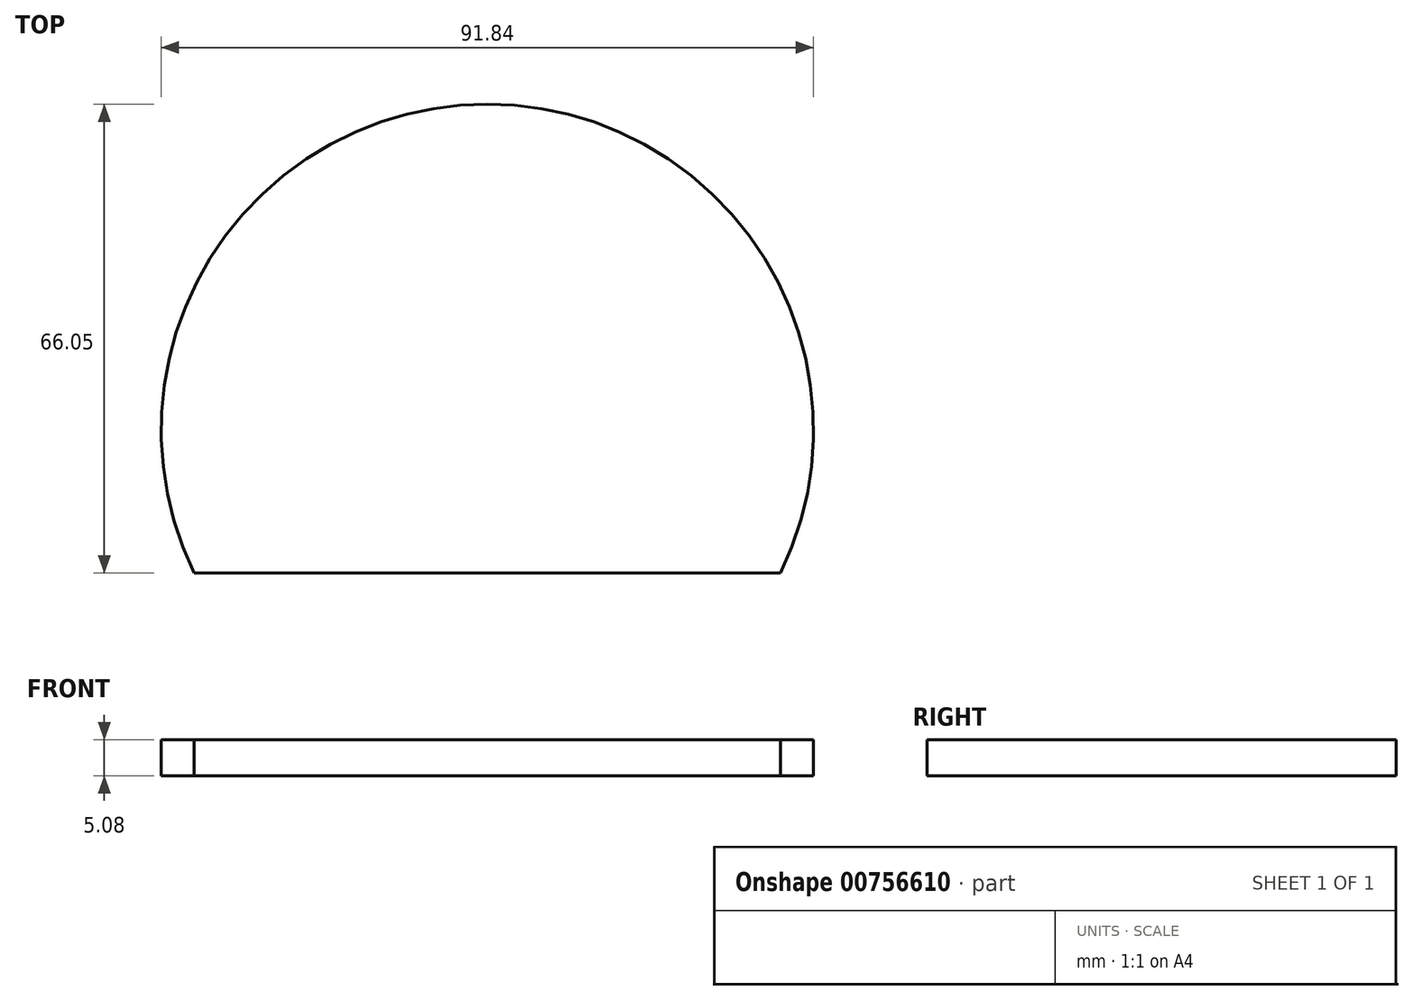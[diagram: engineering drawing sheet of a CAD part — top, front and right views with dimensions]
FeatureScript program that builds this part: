
annotation { "Feature Type Name" : "Feature", "Feature Type Description" : "" }
export const myFeature = defineFeature(function(context is Context, id is Id, definition is map)
    precondition{}
    {
        {
            var Q0;
            Q0=qCreatedBy(makeId("Top.planeOp"),FACE);
            var sketch = newSketch(context, id + "F0", { "sketchPlane" : qUnion([Q0])});
            skArc(sketch, "E0", {"start": v(28.74, -10.41) * mm, "mid": v(-12.54, 33.84) * mm, "end": v(-53.81, -10.41) * mm});
            skArc(sketch, "E1", {"start": v(28.56, -27.66) * mm, "mid": v(-12.72, 38.39) * mm, "end": v(-54, -27.66) * mm});
            skLineSegment(sketch, "E2", {"start": v(-53.81, -10.41) * mm, "end": v(-54, -27.66) * mm});
            skLineSegment(sketch, "E3", {"start": v(28.74, -10.41) * mm, "end": v(28.56, -27.66) * mm});
            skLineSegment(sketch, "E4", {"start": v(-54, -27.66) * mm, "end": v(28.56, -27.66) * mm});
            skSolve(sketch);
        }
        {
            var Q0;
            Q0=makeQuery(id+"F0.imprint","IMPRINT",FACE,{"disambiguationData":[TD([[makeQuery(id+"F0.imprint","IMPRINT",EDGE,{"derivedFrom":sQuery(id+"F0.wireOp",EDGE,"E0")}),-1.0]])]});
            var Q1;
            Q1=makeQuery(id+"F0.imprint","IMPRINT",FACE,{"disambiguationData":[TD([[makeQuery(id+"F0.imprint","IMPRINT",EDGE,{"derivedFrom":sQuery(id+"F0.wireOp",EDGE,"E0")}),1.0]])]});
            extrude(context, id + "F1", {"entities" : qUnion([Q0, Q1]), "depth" : 5.08 * mm, "offsetDistance" : 25.4 * mm});
        }
    });
